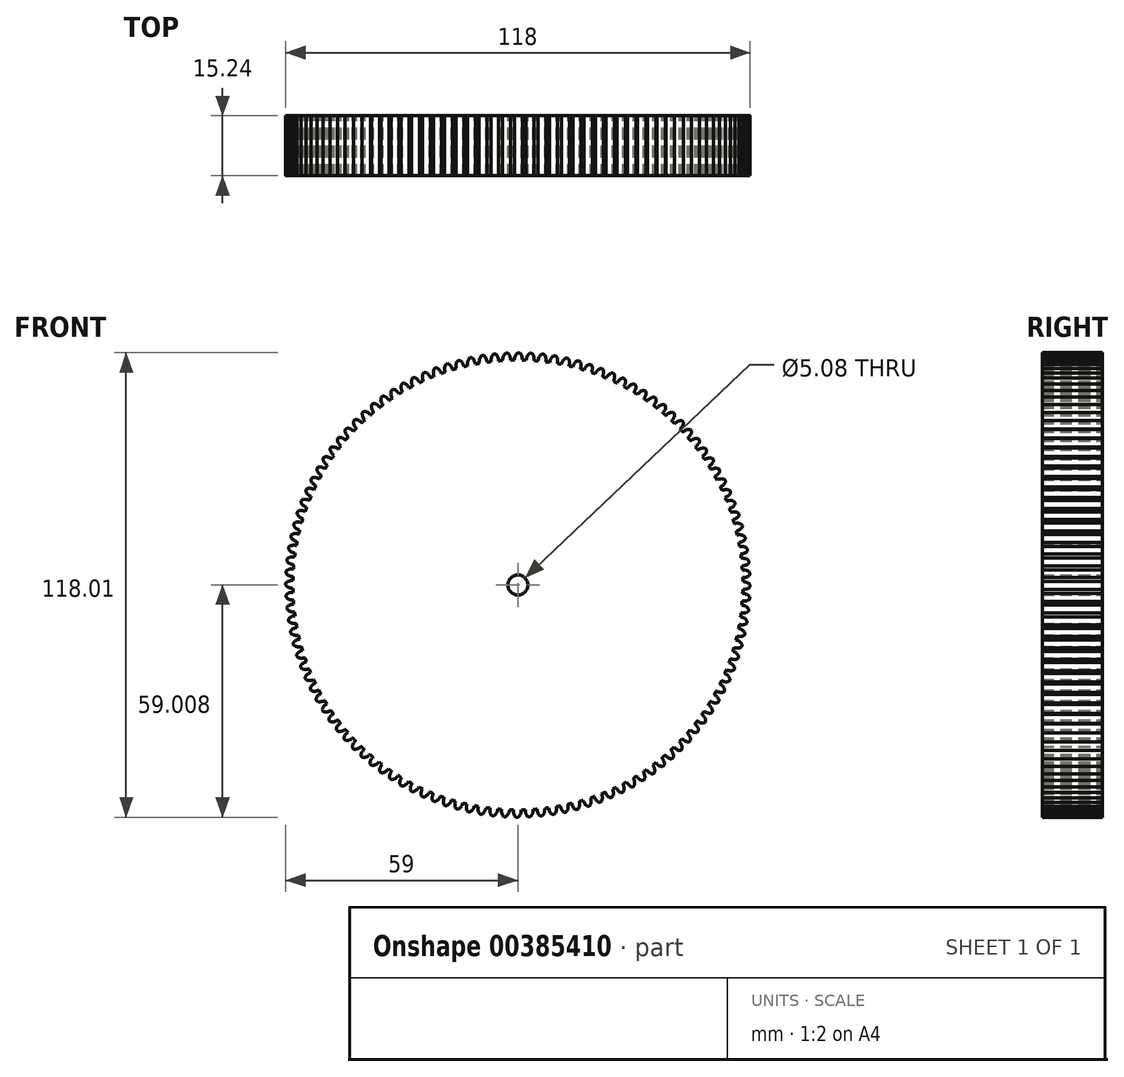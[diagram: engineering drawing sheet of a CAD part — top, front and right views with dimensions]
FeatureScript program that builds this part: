
annotation { "Feature Type Name" : "Feature", "Feature Type Description" : "" }
export const myFeature = defineFeature(function(context is Context, id is Id, definition is map)
    precondition{}
    {
        {
            var Q0;
            Q0=qCreatedBy(makeId("Front.planeOp"),FACE);
            var sketch = newSketch(context, id + "F0", { "sketchPlane" : qUnion([Q0])});
            skCircle(sketch, "E0", {"center": v(16.02, 34.67) * mm, "radius": 57.15 * mm});
            skEllipticalArc(sketch, "E1.67.0", {});
            skEllipticalArc(sketch, "E2.1.0", {});
            skEllipticalArc(sketch, "E2.2.0", {});
            skEllipticalArc(sketch, "E2.3.0", {});
            skEllipticalArc(sketch, "E2.4.0", {});
            skEllipticalArc(sketch, "E2.5.0", {});
            skEllipticalArc(sketch, "E2.6.0", {});
            skEllipticalArc(sketch, "E2.7.0", {});
            skEllipticalArc(sketch, "E2.8.0", {});
            skEllipticalArc(sketch, "E2.9.0", {});
            skEllipticalArc(sketch, "E2.10.0", {});
            skEllipticalArc(sketch, "E2.11.0", {});
            skEllipticalArc(sketch, "E2.12.0", {});
            skEllipticalArc(sketch, "E2.13.0", {});
            skEllipticalArc(sketch, "E2.14.0", {});
            skEllipticalArc(sketch, "E2.15.0", {});
            skEllipticalArc(sketch, "E2.16.0", {});
            skEllipticalArc(sketch, "E2.17.0", {});
            skEllipticalArc(sketch, "E2.18.0", {});
            skEllipticalArc(sketch, "E2.19.0", {});
            skEllipticalArc(sketch, "E2.20.0", {});
            skEllipticalArc(sketch, "E2.21.0", {});
            skEllipticalArc(sketch, "E2.22.0", {});
            skEllipticalArc(sketch, "E2.23.0", {});
            skEllipticalArc(sketch, "E2.24.0", {});
            skEllipticalArc(sketch, "E2.25.0", {});
            skEllipticalArc(sketch, "E2.26.0", {});
            skEllipticalArc(sketch, "E2.27.0", {});
            skEllipticalArc(sketch, "E2.28.0", {});
            skEllipticalArc(sketch, "E2.29.0", {});
            skEllipticalArc(sketch, "E2.30.0", {});
            skEllipticalArc(sketch, "E2.31.0", {});
            skEllipticalArc(sketch, "E2.32.0", {});
            skEllipticalArc(sketch, "E2.33.0", {});
            skEllipticalArc(sketch, "E2.34.0", {});
            skEllipticalArc(sketch, "E2.35.0", {});
            skEllipticalArc(sketch, "E2.36.0", {});
            skEllipticalArc(sketch, "E2.37.0", {});
            skEllipticalArc(sketch, "E2.38.0", {});
            skEllipticalArc(sketch, "E2.39.0", {});
            skEllipticalArc(sketch, "E2.40.0", {});
            skEllipticalArc(sketch, "E2.41.0", {});
            skEllipticalArc(sketch, "E2.42.0", {});
            skEllipticalArc(sketch, "E2.43.0", {});
            skEllipticalArc(sketch, "E2.44.0", {});
            skEllipticalArc(sketch, "E2.45.0", {});
            skEllipticalArc(sketch, "E2.46.0", {});
            skEllipticalArc(sketch, "E2.47.0", {});
            skEllipticalArc(sketch, "E2.48.0", {});
            skEllipticalArc(sketch, "E2.49.0", {});
            skEllipticalArc(sketch, "E2.50.0", {});
            skEllipticalArc(sketch, "E2.51.0", {});
            skEllipticalArc(sketch, "E2.52.0", {});
            skEllipticalArc(sketch, "E2.53.0", {});
            skEllipticalArc(sketch, "E2.54.0", {});
            skEllipticalArc(sketch, "E2.55.0", {});
            skEllipticalArc(sketch, "E2.56.0", {});
            skEllipticalArc(sketch, "E2.57.0", {});
            skEllipticalArc(sketch, "E2.58.0", {});
            skEllipticalArc(sketch, "E2.59.0", {});
            skEllipticalArc(sketch, "E2.60.0", {});
            skEllipticalArc(sketch, "E2.61.0", {});
            skEllipticalArc(sketch, "E2.62.0", {});
            skEllipticalArc(sketch, "E2.63.0", {});
            skEllipticalArc(sketch, "E2.64.0", {});
            skEllipticalArc(sketch, "E2.65.0", {});
            skEllipticalArc(sketch, "E2.66.0", {});
            skEllipticalArc(sketch, "E2.67.0", {});
            skEllipticalArc(sketch, "E2.68.0", {});
            skEllipticalArc(sketch, "E2.69.0", {});
            skEllipticalArc(sketch, "E2.70.0", {});
            skEllipticalArc(sketch, "E2.71.0", {});
            skEllipticalArc(sketch, "E2.72.0", {});
            skEllipticalArc(sketch, "E2.73.0", {});
            skEllipticalArc(sketch, "E2.74.0", {});
            skEllipticalArc(sketch, "E2.75.0", {});
            skEllipticalArc(sketch, "E2.76.0", {});
            skEllipticalArc(sketch, "E2.77.0", {});
            skEllipticalArc(sketch, "E2.78.0", {});
            skEllipticalArc(sketch, "E2.79.0", {});
            skEllipticalArc(sketch, "E2.80.0", {});
            skEllipticalArc(sketch, "E2.81.0", {});
            skEllipticalArc(sketch, "E2.82.0", {});
            skEllipticalArc(sketch, "E2.83.0", {});
            skEllipticalArc(sketch, "E2.84.0", {});
            skEllipticalArc(sketch, "E2.85.0", {});
            skEllipticalArc(sketch, "E2.86.0", {});
            skEllipticalArc(sketch, "E2.87.0", {});
            skEllipticalArc(sketch, "E2.88.0", {});
            skEllipticalArc(sketch, "E2.89.0", {});
            skEllipticalArc(sketch, "E2.90.0", {});
            skEllipticalArc(sketch, "E2.91.0", {});
            skEllipticalArc(sketch, "E2.92.0", {});
            skEllipticalArc(sketch, "E2.93.0", {});
            skEllipticalArc(sketch, "E2.94.0", {});
            skEllipticalArc(sketch, "E2.95.0", {});
            skEllipticalArc(sketch, "E2.96.0", {});
            skEllipticalArc(sketch, "E2.97.0", {});
            skEllipticalArc(sketch, "E2.98.0", {});
            skEllipticalArc(sketch, "E2.99.0", {});
            skEllipticalArc(sketch, "E2.100.0", {});
            skEllipticalArc(sketch, "E2.101.0", {});
            skEllipticalArc(sketch, "E2.102.0", {});
            skEllipticalArc(sketch, "E2.103.0", {});
            skEllipticalArc(sketch, "E2.104.0", {});
            skEllipticalArc(sketch, "E2.105.0", {});
            skEllipticalArc(sketch, "E2.106.0", {});
            skEllipticalArc(sketch, "E2.107.0", {});
            skEllipticalArc(sketch, "E2.108.0", {});
            skEllipticalArc(sketch, "E2.109.0", {});
            skEllipticalArc(sketch, "E2.110.0", {});
            skEllipticalArc(sketch, "E2.111.0", {});
            skEllipticalArc(sketch, "E2.112.0", {});
            skEllipticalArc(sketch, "E2.113.0", {});
            skEllipticalArc(sketch, "E2.114.0", {});
            skEllipticalArc(sketch, "E2.115.0", {});
            skEllipticalArc(sketch, "E2.116.0", {});
            skEllipticalArc(sketch, "E2.117.0", {});
            skEllipticalArc(sketch, "E2.118.0", {});
            skEllipticalArc(sketch, "E2.119.0", {});
            skCircle(sketch, "E3", {"center": v(16.02, 34.67) * mm, "radius": 2.54 * mm});
            const initialGuessF0  = {"E1.67.0": [0.06232418559064743, 0.06816446779273053, -0.8526401643540926, -0.5224985647159486, 0.0018570975044160444, 0.0009917459338206558, 1.604712424427073, 4.760295241054115], "E2.1.0": [0.06050764237135643, 0.07054194239397373, -0.8241261886220159, -0.5664062369248325, 0.0018570975044160444, 0.0009917459338206558, 1.6047124244270745, 4.760295241054114], "E2.2.0": [0.058569161254714903, 0.07282108822246579, -0.7933533402912356, -0.6087614290087203, 0.0018570975044160444, 0.0009917459338206558, 1.6047124244270745, 4.760295241054114], "E2.3.0": [0.05651405548272141, 0.07499565829791235, -0.7604059656000315, -0.6494480483301833, 0.0018570975044160444, 0.0009917459338206558, 1.6047124244270745, 4.760295241054114], "E2.4.0": [0.05434795795744832, 0.07705969227488907, -0.725374371012288, -0.6883545756937536, 0.0018570975044160444, 0.0009917459338206558, 1.6047124244270745, 4.760295241054114], "E2.5.0": [0.052076805801648814, 0.07900753277973432, -0.6883545756937544, -0.7253743710122873, 0.0018570975044160444, 0.0009917459338206558, 1.6047124244270745, 4.760295241054114], "E2.6.0": [0.04970682408551609, 0.08083384091701708, -0.649448048330184, -0.7604059656000308, 0.0018570975044160444, 0.0009917459338206558, 1.6047124244270745, 4.760295241054114], "E2.7.0": [0.04724450876419866, 0.08253361090307815, -0.6087614290087211, -0.793353340291235, 0.0018570975044160444, 0.0009917459338206558, 1.6047124244270745, 4.760295241054114], "E2.8.0": [0.04469660887283881, 0.0841021837865353, -0.5664062369248333, -0.8241261886220155, 0.0018570975044160444, 0.0009917459338206558, 1.6047124244270745, 4.760295241054114], "E2.9.0": [0.04207010802793642, 0.08553526021814514, -0.5224985647159492, -0.852640164354092, 0.0018570975044160444, 0.0009917459338206558, 1.6047124244270745, 4.760295241054114], "E2.10.0": [0.03937220528574152, 0.08682891223502057, -0.477158760259609, -0.8788171126619653, 0.0018570975044160444, 0.0009917459338206558, 1.6047124244270745, 4.760295241054114], "E2.11.0": [0.036610295410141554, 0.08797959402690392, -0.43051109680829575, -0.9025852843498605, 0.0018570975044160444, 0.0009917459338206558, 1.6047124244270745, 4.760295241054114], "E2.12.0": [0.03379194860412753, 0.08898415165498663, -0.3826834323650903, -0.9238795325112867, 0.0018570975044160444, 0.0009917459338206558, 1.6047124244270745, 4.760295241054114], "E2.13.0": [0.030924889760393856, 0.08983983169663604, -0.3338068592337713, -0.9426414910921783, 0.0018570975044160444, 0.0009917459338206558, 1.6047124244270745, 4.760295241054114], "E2.14.0": [0.028016977287944382, 0.09054428879233556, -0.28401534470392303, -0.958819734868193, 0.0018570975044160444, 0.0009917459338206558, 1.6047124244270745, 4.760295241054114], "E2.15.0": [0.025076181572739588, 0.09109559207415213, -0.23344536385590592, -0.9723699203976766, 0.0018570975044160444, 0.0009917459338206558, 1.6047124244270745, 4.760295241054114], "E2.16.0": [0.02211056313142264, 0.09149223045811086, -0.18223552549214797, -0.9832549075639546, 0.0018570975044160441, 0.0009917459338206556, 1.6047124244270745, 4.760295241054114], "E2.17.0": [0.01912825051800357, 0.09173311678597135, -0.1305261922200521, -0.9914448613738105, 0.0018570975044160444, 0.0009917459338206558, 1.6047124244270745, 4.760295241054114], "E2.18.0": [0.016137418044057758, 0.09181759080505272, -0.07845909572784543, -0.996917333733128, 0.0018570975044160444, 0.0009917459338206558, 1.6047124244270745, 4.760295241054114], "E2.19.0": [0.013146263373506072, 0.09174542097794039, -0.026176948307873767, -0.9996573249755574, 0.0018570975044160444, 0.0009917459338206558, 1.6047124244270745, 4.760295241054114], "E2.20.0": [0.010162985053387887, 0.09151680511711405, 0.0261769483078726, -0.9996573249755575, 0.0018570975044160444, 0.0009917459338206558, 1.6047124244270745, 4.760295241054114], "E2.21.0": [0.007195760042213499, 0.09113236984275726, 0.07845909572784444, -0.9969173337331282, 0.0018570975044160444, 0.0009917459338206558, 1.6047124244270745, 4.760295241054114], "E2.22.0": [0.00425272129748927, 0.09059316886523532, 0.13052619222005102, -0.9914448613738105, 0.0018570975044160444, 0.0009917459338206558, 1.6047124244270745, 4.760295241054114], "E2.23.0": [0.0013419354838463682, 0.0899006800969482, 0.18223552549214694, -0.9832549075639547, 0.0018570975044160444, 0.0009917459338206558, 1.6047124244270745, 4.760295241054114], "E2.24.0": [-0.0015286191371262497, 0.08905680160147544, 0.23344536385590497, -0.9723699203976768, 0.0018570975044160444, 0.0009917459338206558, 1.6047124244270745, 4.760295241054114], "E2.25.0": [-0.004351074574742313, 0.08806384639111592, 0.28401534470392226, -0.9588197348681933, 0.0018570975044160444, 0.0009917459338206558, 1.6047124244270745, 4.760295241054114], "E2.26.0": [-0.00711769467483378, 0.0869245360870817, 0.33380685923377057, -0.9426414910921785, 0.0018570975044160444, 0.0009917459338206558, 1.6047124244270745, 4.760295241054114], "E2.27.0": [-0.009820896324011695, 0.0856419934597237, 0.3826834323650893, -0.923879532511287, 0.0018570975044160444, 0.0009917459338206558, 1.6047124244270745, 4.760295241054114], "E2.28.0": [-0.012453270234452911, 0.08421973386923504, 0.43051109680829486, -0.902585284349861, 0.0018570975044160444, 0.0009917459338206558, 1.6047124244270745, 4.760295241054114], "E2.29.0": [-0.015007601252242986, 0.0826616556302932, 0.47715876025960824, -0.8788171126619657, 0.0018570975044160444, 0.0009917459338206558, 1.6047124244270745, 4.760295241054114], "E2.30.0": [-0.017476888133611514, 0.08097202932705043, 0.5224985647159484, -0.8526401643540927, 0.0018570975044160444, 0.0009917459338206558, 1.6047124244270745, 4.760295241054114], "E2.31.0": [-0.019854362734854705, 0.07915548610775944, 0.5664062369248323, -0.824126188622016, 0.0018570975044160441, 0.0009917459338206556, 1.6047124244270745, 4.760295241054114], "E2.32.0": [-0.022133508563346782, 0.07721700499111792, 0.6087614290087202, -0.7933533402912355, 0.0018570975044160444, 0.0009917459338206558, 1.6047124244270745, 4.760295241054114], "E2.33.0": [-0.02430807863879334, 0.0751618992191244, 0.6494480483301833, -0.7604059656000315, 0.0018570975044160444, 0.0009917459338206558, 1.6047124244270745, 4.760295241054114], "E2.34.0": [-0.02637211261577007, 0.07299580169385131, 0.6883545756937536, -0.725374371012288, 0.0018570975044160444, 0.0009917459338206558, 1.6047124244270745, 4.760295241054114], "E2.35.0": [-0.02831995312061531, 0.0707246495380518, 0.7253743710122873, -0.6883545756937545, 0.0018570975044160444, 0.0009917459338206558, 1.6047124244270745, 4.760295241054114], "E2.36.0": [-0.030146261257898065, 0.06835466782191907, 0.7604059656000306, -0.649448048330184, 0.0018570975044160444, 0.0009917459338206558, 1.6047124244270745, 4.760295241054114], "E2.37.0": [-0.031846031243959134, 0.06589235250060166, 0.793353340291235, -0.6087614290087211, 0.0018570975044160444, 0.0009917459338206558, 1.6047124244270745, 4.760295241054114], "E2.38.0": [-0.033414604127416286, 0.0633444526092418, 0.8241261886220153, -0.5664062369248334, 0.0018570975044160444, 0.0009917459338206558, 1.6047124244270745, 4.760295241054114], "E2.39.0": [-0.034847680559026116, 0.06071795176433942, 0.8526401643540921, -0.5224985647159495, 0.0018570975044160444, 0.0009917459338206558, 1.6047124244270745, 4.760295241054114], "E2.40.0": [-0.03614133257590154, 0.05802004902214452, 0.8788171126619653, -0.47715876025960907, 0.0018570975044160444, 0.0009917459338206558, 1.6047124244270745, 4.760295241054114], "E2.41.0": [-0.03729201436778491, 0.05525813914654456, 0.9025852843498603, -0.43051109680829586, 0.0018570975044160444, 0.0009917459338206558, 1.6047124244270745, 4.760295241054114], "E2.42.0": [-0.03829657199586763, 0.05243979234053052, 0.9238795325112867, -0.38268343236509034, 0.0018570975044160441, 0.0009917459338206556, 1.6047124244270745, 4.760295241054114], "E2.43.0": [-0.03915225203751702, 0.049572733496796854, 0.9426414910921783, -0.33380685923377157, 0.0018570975044160444, 0.0009917459338206558, 1.6047124244270745, 4.760295241054114], "E2.44.0": [-0.039856709133216546, 0.0466648210243474, 0.9588197348681928, -0.28401534470392337, 0.0018570975044160444, 0.0009917459338206558, 1.6047124244270745, 4.760295241054114], "E2.45.0": [-0.04040801241503312, 0.04372402530914258, 0.9723699203976766, -0.23344536385590592, 0.0018570975044160444, 0.0009917459338206558, 1.6047124244270745, 4.760295241054114], "E2.46.0": [-0.04080465079899185, 0.040758406867825635, 0.9832549075639545, -0.18223552549214814, 0.0018570975044160444, 0.0009917459338206558, 1.6047124244270745, 4.760295241054114], "E2.47.0": [-0.04104553712685233, 0.03777609425440656, 0.9914448613738105, -0.130526192220052, 0.0018570975044160444, 0.0009917459338206558, 1.6047124244270745, 4.760295241054114], "E2.48.0": [-0.04113001114593371, 0.034785261780460756, 0.9969173337331281, -0.07845909572784561, 0.0018570975044160444, 0.0009917459338206558, 1.6047124244270745, 4.760295241054114], "E2.49.0": [-0.0410578413188214, 0.03179410710990907, 0.9996573249755573, -0.02617694830787387, 0.0018570975044160444, 0.0009917459338206558, 1.6047124244270745, 4.760295241054114], "E2.50.0": [-0.04082922545799503, 0.02881082878979086, 0.9996573249755575, 0.026176948307872823, 0.0018570975044160444, 0.0009917459338206558, 1.6047124244270745, 4.760295241054114], "E2.51.0": [-0.04044479018363825, 0.025843603778616497, 0.9969173337331282, 0.07845909572784439, 0.0018570975044160444, 0.0009917459338206558, 1.6047124244270745, 4.760295241054114], "E2.52.0": [-0.03990558920611631, 0.022900565033892248, 0.9914448613738106, 0.13052619222005138, 0.0018570975044160444, 0.0009917459338206558, 1.6047124244270745, 4.760295241054114], "E2.53.0": [-0.039213100437829176, 0.019989779220249353, 0.9832549075639548, 0.18223552549214708, 0.0018570975044160444, 0.0009917459338206558, 1.6047124244270745, 4.760295241054114], "E2.54.0": [-0.03836922194235645, 0.01711922459927674, 0.9723699203976768, 0.23344536385590497, 0.0018570975044160444, 0.0009917459338206558, 1.6047124244270745, 4.760295241054114], "E2.55.0": [-0.0373762667319969, 0.014296769161660672, 0.9588197348681933, 0.2840153447039224, 0.0018570975044160444, 0.0009917459338206558, 1.6047124244270745, 4.760295241054114], "E2.56.0": [-0.03623695642796271, 0.011530149061569218, 0.9426414910921785, 0.3338068592337705, 0.0018570975044160444, 0.0009917459338206558, 1.6047124244270745, 4.760295241054114], "E2.57.0": [-0.0349544138006047, 0.00882694741239131, 0.923879532511287, 0.3826834323650892, 0.0018570975044160444, 0.0009917459338206558, 1.6047124244270745, 4.760295241054114], "E2.58.0": [-0.03353215421011604, 0.0061945735019500806, 0.9025852843498609, 0.430511096808295, 0.0018570975044160444, 0.0009917459338206558, 1.6047124244270745, 4.760295241054114], "E2.59.0": [-0.03197407597117419, 0.0036402424841600056, 0.8788171126619657, 0.4771587602596082, 0.0018570975044160441, 0.0009917459338206556, 1.6047124244270745, 4.760295241054114], "E2.60.0": [-0.030284449667931437, 0.0011709556027914986, 0.8526401643540927, 0.522498564715948, 0.0018570975044160444, 0.0009917459338206558, 1.6047124244270745, 4.760295241054114], "E2.61.0": [-0.028467906448640425, -0.0012065189984517138, 0.824126188622016, 0.5664062369248323, 0.0018570975044160441, 0.0009917459338206556, 1.6047124244270745, 4.760295241054114], "E2.62.0": [-0.02652942533199891, -0.0034856648269437907, 0.7933533402912358, 0.60876142900872, 0.0018570975044160444, 0.0009917459338206558, 1.6047124244270745, 4.760295241054114], "E2.63.0": [-0.0244743195600054, -0.005660234902390343, 0.7604059656000314, 0.6494480483301832, 0.0018570975044160444, 0.0009917459338206558, 1.6047124244270745, 4.760295241054114], "E2.64.0": [-0.02230822203473231, -0.007724268879367058, 0.7253743710122882, 0.6883545756937535, 0.0018570975044160444, 0.0009917459338206558, 1.6047124244270745, 4.760295241054114], "E2.65.0": [-0.020037069878932817, -0.009672109384212313, 0.6883545756937546, 0.7253743710122871, 0.0018570975044160444, 0.0009917459338206558, 1.6047124244270745, 4.760295241054114], "E2.66.0": [-0.017667088162800083, -0.011498417521495066, 0.6494480483301841, 0.7604059656000306, 0.0018570975044160444, 0.0009917459338206558, 1.6047124244270745, 4.760295241054114], "E2.67.0": [-0.015204772841482653, -0.01319818750755615, 0.6087614290087212, 0.7933533402912347, 0.0018570975044160444, 0.0009917459338206558, 1.6047124244270745, 4.760295241054114], "E2.68.0": [-0.012656872950122793, -0.014766760391013309, 0.5664062369248332, 0.8241261886220154, 0.0018570975044160441, 0.0009917459338206556, 1.6047124244270745, 4.760295241054114], "E2.69.0": [-0.010030372105220406, -0.01619983682262313, 0.5224985647159495, 0.8526401643540921, 0.0018570975044160444, 0.0009917459338206558, 1.6047124244270745, 4.760295241054114], "E2.70.0": [-0.007332469363025519, -0.01749348883949854, 0.4771587602596091, 0.878817112661965, 0.0018570975044160444, 0.0009917459338206558, 1.6047124244270745, 4.760295241054114], "E2.71.0": [-0.0045705594874255375, -0.01864417063138195, 0.4305110968082957, 0.9025852843498605, 0.0018570975044160444, 0.0009917459338206558, 1.6047124244270745, 4.760295241054114], "E2.72.0": [-0.0017522126814115205, -0.019648728259464635, 0.38268343236509034, 0.9238795325112865, 0.0018570975044160444, 0.0009917459338206558, 1.6047124244270745, 4.760295241054114], "E2.73.0": [0.0011148461623221445, -0.020504408301114038, 0.3338068592337716, 0.9426414910921782, 0.0018570975044160441, 0.0009917459338206556, 1.6047124244270745, 4.760295241054114], "E2.74.0": [0.004022758634771632, -0.02120886539681356, 0.28401534470392303, 0.958819734868193, 0.0018570975044160444, 0.0009917459338206558, 1.6047124244270745, 4.760295241054114], "E2.75.0": [0.00696355434997642, -0.02176016867863012, 0.23344536385590597, 0.9723699203976764, 0.0018570975044160444, 0.0009917459338206558, 1.6047124244270745, 4.760295241054114], "E2.76.0": [0.009929172791293364, -0.02215680706258885, 0.18223552549214825, 0.9832549075639546, 0.0018570975044160444, 0.0009917459338206558, 1.6047124244270745, 4.760295241054114], "E2.77.0": [0.012911485404712417, -0.02239769339044935, 0.13052619222005246, 0.9914448613738103, 0.0018570975044160444, 0.0009917459338206558, 1.6047124244270745, 4.760295241054114], "E2.78.0": [0.01590231787865825, -0.022482167409530726, 0.07845909572784561, 0.9969173337331281, 0.0018570975044160444, 0.0009917459338206558, 1.6047124244270745, 4.760295241054114], "E2.79.0": [0.018893472549209957, -0.022409997582418406, 0.02617694830787349, 0.9996573249755574, 0.0018570975044160444, 0.0009917459338206558, 1.6047124244270745, 4.760295241054114], "E2.80.0": [0.021876750869328106, -0.022181381721592036, -0.026176948307872212, 0.9996573249755574, 0.0018570975044160444, 0.0009917459338206558, 1.6047124244270745, 4.760295241054114], "E2.81.0": [0.02484397588050251, -0.02179694644723526, -0.07845909572784433, 0.9969173337331282, 0.0018570975044160444, 0.0009917459338206558, 1.6047124244270745, 4.760295241054114], "E2.82.0": [0.027787014625226703, -0.02125774546971332, -0.13052619222005044, 0.9914448613738106, 0.0018570975044160444, 0.0009917459338206558, 1.6047124244270745, 4.760295241054114], "E2.83.0": [0.030697800438869674, -0.020565256701426185, -0.18223552549214747, 0.9832549075639547, 0.0018570975044160444, 0.0009917459338206558, 1.6047124244270745, 4.760295241054114], "E2.84.0": [0.033568355059842264, -0.01972137820595346, -0.23344536385590492, 0.9723699203976769, 0.0018570975044160444, 0.0009917459338206558, 1.6047124244270745, 4.760295241054114], "E2.85.0": [0.036390810497458334, -0.018728422995593907, -0.28401534470392237, 0.9588197348681933, 0.0018570975044160444, 0.0009917459338206558, 1.6047124244270745, 4.760295241054114], "E2.86.0": [0.03915743059754975, -0.01758911269155973, -0.3338068592337701, 0.9426414910921789, 0.0018570975044160444, 0.0009917459338206558, 1.6047124244270745, 4.760295241054114], "E2.87.0": [0.041860632246727696, -0.016306570064201713, -0.38268343236508917, 0.923879532511287, 0.0018570975044160441, 0.0009917459338206556, 1.6047124244270745, 4.760295241054114], "E2.88.0": [0.04449300615716889, -0.014884310473713067, -0.4305110968082941, 0.9025852843498612, 0.0018570975044160444, 0.0009917459338206558, 1.6047124244270745, 4.760295241054114], "E2.89.0": [0.04704733717495903, -0.013326232234771196, -0.4771587602596084, 0.8788171126619654, 0.0018570975044160444, 0.0009917459338206558, 1.6047124244270745, 4.760295241054114], "E2.90.0": [0.04951662405632752, -0.011636605931528432, -0.5224985647159484, 0.8526401643540925, 0.0018570975044160444, 0.0009917459338206558, 1.6047124244270745, 4.760295241054114], "E2.91.0": [0.05189409865757074, -0.009820062712237412, -0.5664062369248326, 0.8241261886220158, 0.0018570975044160444, 0.0009917459338206558, 1.6047124244270745, 4.760295241054114], "E2.92.0": [0.054173244486062776, -0.007881581595595918, -0.60876142900872, 0.7933533402912358, 0.0018570975044160444, 0.0009917459338206558, 1.6047124244270745, 4.760295241054114], "E2.93.0": [0.05634781456150935, -0.005826475823602413, -0.6494480483301831, 0.7604059656000314, 0.0018570975044160444, 0.0009917459338206558, 1.6047124244270745, 4.760295241054114], "E2.94.0": [0.05841184853848607, -0.0036603782983293046, -0.6883545756937538, 0.7253743710122879, 0.0018570975044160444, 0.0009917459338206558, 1.6047124244270745, 4.760295241054114], "E2.95.0": [0.06035968904333134, -0.001389226142529787, -0.7253743710122877, 0.688354575693754, 0.0018570975044160444, 0.0009917459338206558, 1.6047124244270745, 4.760295241054114], "E2.96.0": [0.06218599718061408, 0.000980755573602915, -0.7604059656000307, 0.6494480483301842, 0.0018570975044160444, 0.0009917459338206558, 1.6047124244270745, 4.760295241054114], "E2.97.0": [0.06388576716667513, 0.003443070894920311, -0.7933533402912346, 0.6087614290087217, 0.0018570975044160444, 0.0009917459338206558, 1.6047124244270745, 4.760295241054114], "E2.98.0": [0.06545434005013229, 0.005990970786280175, -0.8241261886220153, 0.5664062369248337, 0.0018570975044160444, 0.0009917459338206558, 1.6047124244270745, 4.760295241054114], "E2.99.0": [0.06688741648174212, 0.008617471631182587, -0.852640164354092, 0.5224985647159495, 0.0018570975044160444, 0.0009917459338206558, 1.6047124244270745, 4.760295241054114], "E2.100.0": [0.06818106849861755, 0.011315374373377499, -0.8788171126619653, 0.4771587602596087, 0.0018570975044160444, 0.0009917459338206558, 1.6047124244270745, 4.760295241054114], "E2.101.0": [0.06933175029050093, 0.014077284248977431, -0.9025852843498603, 0.430511096808296, 0.0018570975044160444, 0.0009917459338206558, 1.6047124244270745, 4.760295241054114], "E2.102.0": [0.07033630791858364, 0.016895631054991467, -0.9238795325112865, 0.38268343236509045, 0.0018570975044160444, 0.0009917459338206558, 1.6047124244270745, 4.760295241054114], "E2.103.0": [0.07119198796023304, 0.019762689898725115, -0.9426414910921781, 0.3338068592337721, 0.0018570975044160444, 0.0009917459338206558, 1.6047124244270745, 4.760295241054114], "E2.104.0": [0.07189644505593258, 0.02267060237117464, -0.958819734868193, 0.28401534470392276, 0.0018570975044160444, 0.0009917459338206558, 1.6047124244270745, 4.760295241054114], "E2.105.0": [0.07244774833774914, 0.025611398086379408, -0.9723699203976766, 0.23344536385590609, 0.0018570975044160444, 0.0009917459338206558, 1.6047124244270745, 4.760295241054114], "E2.106.0": [0.07284438672170787, 0.028577016527696376, -0.9832549075639545, 0.1822355254921478, 0.0018570975044160444, 0.0009917459338206558, 1.6047124244270745, 4.760295241054114], "E2.107.0": [0.07308527304956836, 0.03155932914111541, -0.9914448613738103, 0.13052619222005246, 0.0018570975044160444, 0.0009917459338206558, 1.6047124244270745, 4.760295241054114], "E2.108.0": [0.07316974706864973, 0.034550161615061234, -0.996917333733128, 0.0784590957278456, 0.0018570975044160444, 0.0009917459338206558, 1.6047124244270745, 4.760295241054114], "E2.109.0": [0.07309757724153743, 0.03754131628561289, -0.9996573249755574, 0.026176948307874377, 0.0018570975044160444, 0.0009917459338206558, 1.6047124244270745, 4.760295241054114], "E2.110.0": [0.07286896138071103, 0.04052459460573116, -0.9996573249755575, -0.0261769483078731, 0.0018570975044160444, 0.0009917459338206558, 1.6047124244270745, 4.760295241054114], "E2.111.0": [0.07248452610635428, 0.0434918196169055, -0.9969173337331281, -0.07845909572784432, 0.0018570975044160444, 0.0009917459338206558, 1.6047124244270745, 4.760295241054114], "E2.112.0": [0.07194532512883231, 0.04643485836162975, -0.9914448613738105, -0.13052619222005124, 0.0018570975044160444, 0.0009917459338206558, 1.6047124244270745, 4.760295241054114], "E2.113.0": [0.0712528363605452, 0.04934564417527261, -0.983254907563955, -0.18223552549214653, 0.0018570975044160444, 0.0009917459338206558, 1.6047124244270745, 4.760295241054114], "E2.114.0": [0.07040895786507247, 0.05221619879624525, -0.9723699203976769, -0.23344536385590486, 0.0018570975044160444, 0.0009917459338206558, 1.6047124244270745, 4.760295241054114], "E2.115.0": [0.06941600265471293, 0.055038654233861325, -0.9588197348681933, -0.2840153447039223, 0.0018570975044160444, 0.0009917459338206558, 1.6047124244270745, 4.760295241054114], "E2.116.0": [0.06827669235067871, 0.0578052743339528, -0.9426414910921785, -0.33380685923377085, 0.0018570975044160444, 0.0009917459338206558, 1.6047124244270745, 4.760295241054114], "E2.117.0": [0.06699414972332071, 0.06050847598313068, -0.923879532511287, -0.38268343236508917, 0.0018570975044160444, 0.0009917459338206558, 1.6047124244270745, 4.760295241054114], "E2.118.0": [0.06557189013283204, 0.06314084989357192, -0.9025852843498607, -0.4305110968082948, 0.0018570975044160444, 0.0009917459338206558, 1.6047124244270745, 4.760295241054114], "E2.119.0": [0.06401381189389022, 0.06569518091136198, -0.8788171126619658, -0.4771587602596076, 0.0018570975044160444, 0.0009917459338206558, 1.6047124244270745, 4.760295241054114]};
            skSetInitialGuess(sketch, initialGuessF0);
            skSolve(sketch);
        }
        {
            var Q0;
            Q0=qSketchRegion(id+"F0",true);
            extrude(context, id + "F1", {"entities" : qUnion([Q0]), "depth" : 15.24 * mm});
        }
    });
